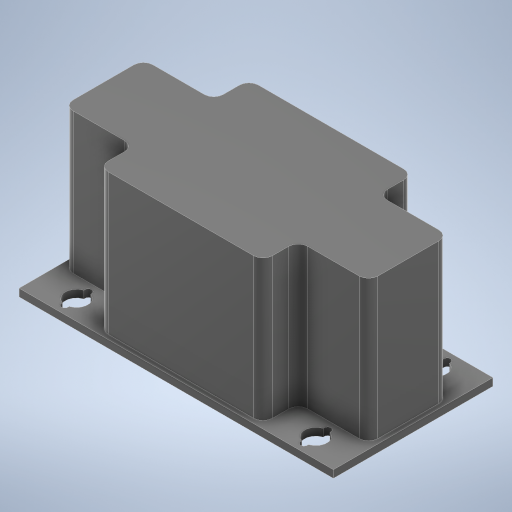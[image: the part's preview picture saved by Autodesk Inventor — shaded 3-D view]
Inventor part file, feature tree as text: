
AUTODESK INVENTOR PART (.ipt)
format: ipt  version: 2024.2 (Build 282272000, 272)  size: 314,368 bytes
history: native  units: mm
features: extrude x2, sketch x1, fillet x1
ambient origin geometry x8: Origin, YZ Plane, XZ Plane, XY Plane, X Axis, Y Axis, Z Axis, Center Point
bodies: Solid1 (feature_tree)
feature tree (4):
  sketch  "Sketch1"  dims[d0=34.0mm d1=67.0mm d7=1.6mm d8=0.0mm d9=31.6mm d10=0.0mm d18=2.0mm d19=4.8mm d33=51.0mm d34=25.5mm d38=1.0mm d43=1.0mm d44=1.0mm d46=6.5mm d47=1.5mm d48=1.0mm d50=16.0mm]
  extrude  "Extrusion1"  Depth=67.0mm
  extrude  "Extrusion2"  Depth=1.6mm TaperAngle=0.0deg
  fillet  "Fillet1"  Radius=31.6mm
